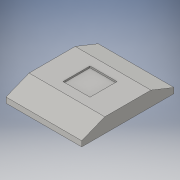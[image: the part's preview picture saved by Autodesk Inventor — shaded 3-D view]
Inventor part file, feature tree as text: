
AUTODESK INVENTOR PART (.ipt)
format: ipt  version: 2016 (Build 200138000, 138)  size: 111,104 bytes
history: native  units: in
note: dims shown in document units (in); Inventor stores cm internally (conversion verified against a paired STEP export)
features: extrude x3, sketch x3
ambient origin geometry x8: Origin, YZ Plane, XZ Plane, XY Plane, X Axis, Y Axis, Z Axis, Center Point
bodies: Solid1 (feature_tree)
feature tree (6):
  extrude  "Extrusion1"  Depth=13.3in
  extrude  "Extrusion2"  Depth=2.56in
  extrude  "Extrusion3"  Depth=0.2812in
  sketch  "Sketch1"  dims[d0=16.2in d1=13.3in]
  sketch  "Sketch2"  dims[d2=2.56in d3=0.0in d4=8.1in]
  sketch  "Sketch3"  dims[d5=0.94in d6=0.94in d7=15.2475in d8=0.0in d9=4.75in d10=4.75in d11=0.2812in d12=0.0in]
